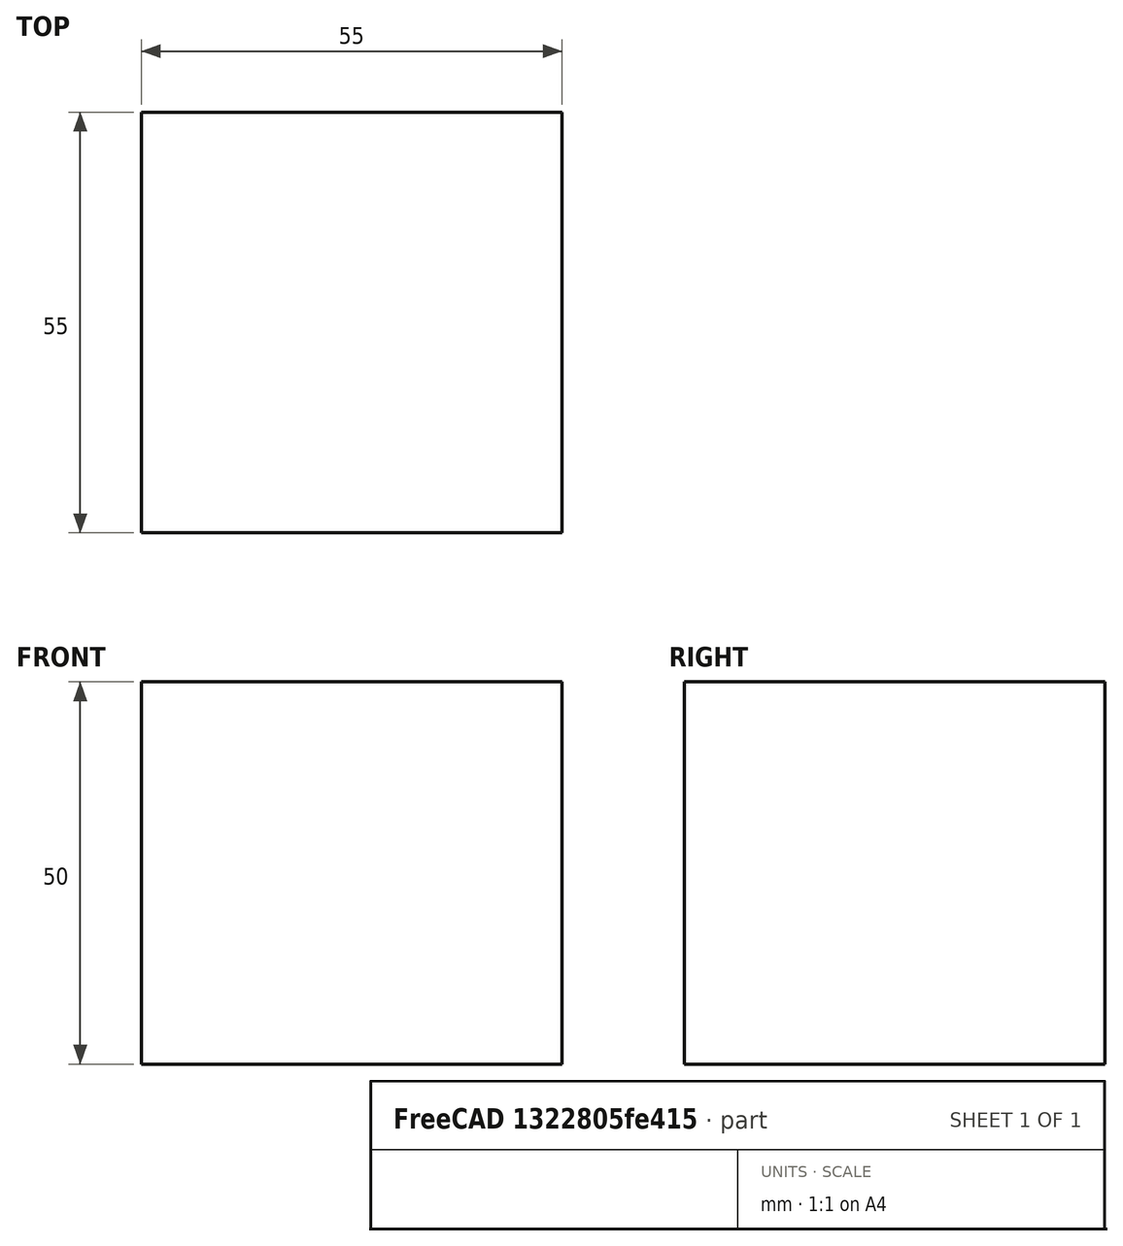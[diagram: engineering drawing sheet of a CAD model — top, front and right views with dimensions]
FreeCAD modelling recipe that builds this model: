
FCSTD DOCUMENT  (FreeCAD 0.15R4671 (Git))
Label: Square Bar 55 EN10059 S235JR
License: All rights reserved
LicenseURL: http://en.wikipedia.org/wiki/All_rights_reserved
objects: Sketcher::SketchObject×1, Part::Extrusion×1
note: 2 computed .brp shape members not serialized (recipe doc carries the construction recipe); baked Part::Feature solids carry a one-line shape summary decoded from their .brp

FEATURE [Sketcher::SketchObject] Sketch
  sketch-geometry (4):
    g0: LineSegment StartX=-27.5 StartY=-27.5 StartZ=0 EndX=27.5 EndY=-27.5 EndZ=0
    g1: LineSegment StartX=27.5 StartY=-27.5 StartZ=0 EndX=27.5 EndY=27.5 EndZ=0
    g2: LineSegment StartX=27.5 StartY=27.5 StartZ=0 EndX=-27.5 EndY=27.5 EndZ=0
    g3: LineSegment StartX=-27.5 StartY=27.5 StartZ=0 EndX=-27.5 EndY=-27.5 EndZ=0
  constraints (12):
    c: Coincident(g0,g1)
    c: Coincident(g1,g2)
    c: Coincident(g2,g3)
    c: Coincident(g3,g0)
    c: Horizontal(g0)
    c: Horizontal(g2)
    c: Vertical(g1)
    c: Vertical(g3)
    c: Symmetric(g1,g0,g-1)
    c: Symmetric(g2,g1,g-2)
    c: Equal(g1,g2)
    c: DistanceY(g1) = 55
FEATURE [Part::Extrusion] Extrude  label="Square Bar 55 EN10059 S235JR"
  Base = -> Sketch
  Dir = (0,0,50)
  Solid = true
